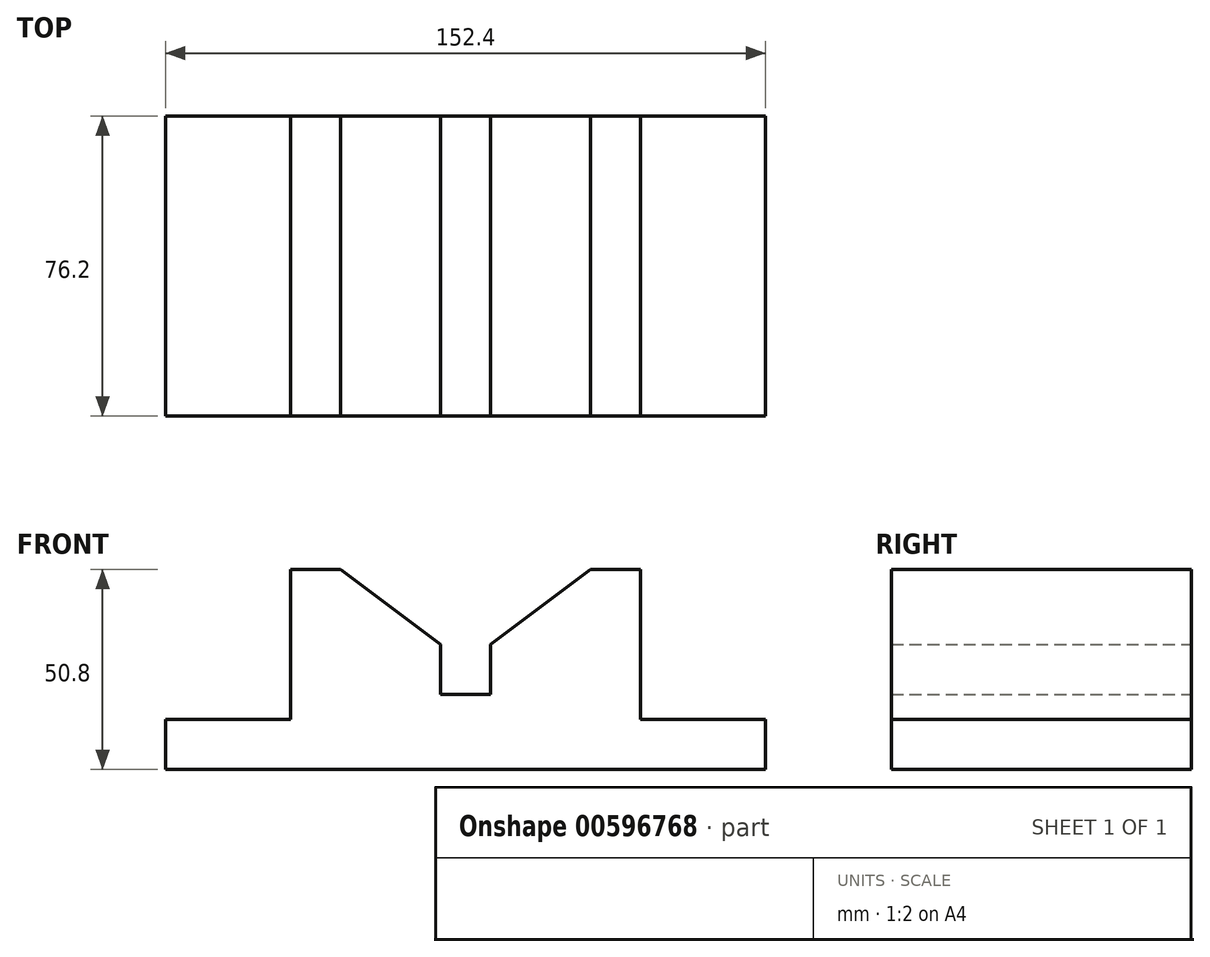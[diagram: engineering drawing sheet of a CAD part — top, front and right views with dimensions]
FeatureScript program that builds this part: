
annotation { "Feature Type Name" : "Feature", "Feature Type Description" : "" }
export const myFeature = defineFeature(function(context is Context, id is Id, definition is map)
    precondition{}
    {
        {
            var Q0;
            Q0=qCreatedBy(makeId("Front.planeOp"),FACE);
            var sketch = newSketch(context, id + "F0", { "sketchPlane" : qUnion([Q0])});
            skLineSegment(sketch, "E0", {"start": v(0, 0) * mm, "end": v(0, 12.7) * mm});
            skLineSegment(sketch, "E1", {"start": v(0, 12.7) * mm, "end": v(31.75, 12.7) * mm});
            skLineSegment(sketch, "E2", {"start": v(31.75, 12.7) * mm, "end": v(31.75, 50.8) * mm});
            skLineSegment(sketch, "E3", {"start": v(31.75, 50.8) * mm, "end": v(44.45, 50.8) * mm});
            skLineSegment(sketch, "E4", {"start": v(44.45, 50.8) * mm, "end": v(69.85, 31.75) * mm});
            skPoint(sketch, "E4.endSnap0", {"position": v(31.75, 31.75) * mm});
            skLineSegment(sketch, "E5", {"start": v(69.85, 31.75) * mm, "end": v(69.85, 19.05) * mm});
            skLineSegment(sketch, "E6", {"start": v(69.85, 19.05) * mm, "end": v(82.55, 19.05) * mm});
            skLineSegment(sketch, "E7", {"start": v(82.55, 19.05) * mm, "end": v(82.55, 31.75) * mm});
            skLineSegment(sketch, "E8", {"start": v(82.55, 31.75) * mm, "end": v(107.95, 50.8) * mm});
            skLineSegment(sketch, "E9", {"start": v(107.95, 50.8) * mm, "end": v(120.65, 50.8) * mm});
            skLineSegment(sketch, "E10", {"start": v(120.65, 50.8) * mm, "end": v(120.65, 12.7) * mm});
            skLineSegment(sketch, "E11", {"start": v(120.65, 12.7) * mm, "end": v(152.4, 12.7) * mm});
            skLineSegment(sketch, "E12", {"start": v(152.4, 12.7) * mm, "end": v(152.4, 0) * mm});
            skLineSegment(sketch, "E13", {"start": v(152.4, 0) * mm, "end": v(0, 0) * mm});
            skLineSegment(sketch, "E14", {"start": v(31.75, 50.8) * mm, "end": v(31.75, 19.05) * mm});
            skLineSegment(sketch, "E15", {"start": v(120.65, 50.8) * mm, "end": v(120.65, 19.05) * mm});
            skSolve(sketch);
        }
        {
            var Q0;
            Q0=makeQuery(id+"F0.imprint","IMPRINT",FACE,{"disambiguationData":[TD([[makeQuery(id+"F0.imprint","IMPRINT",EDGE,{"derivedFrom":sQuery(id+"F0.wireOp",EDGE,"E0")}),-1.0]])]});
            extrude(context, id + "F1", {"entities" : qUnion([Q0]), "depth" : 76.2 * mm, "offsetDistance" : 25.4 * mm});
        }
    });
